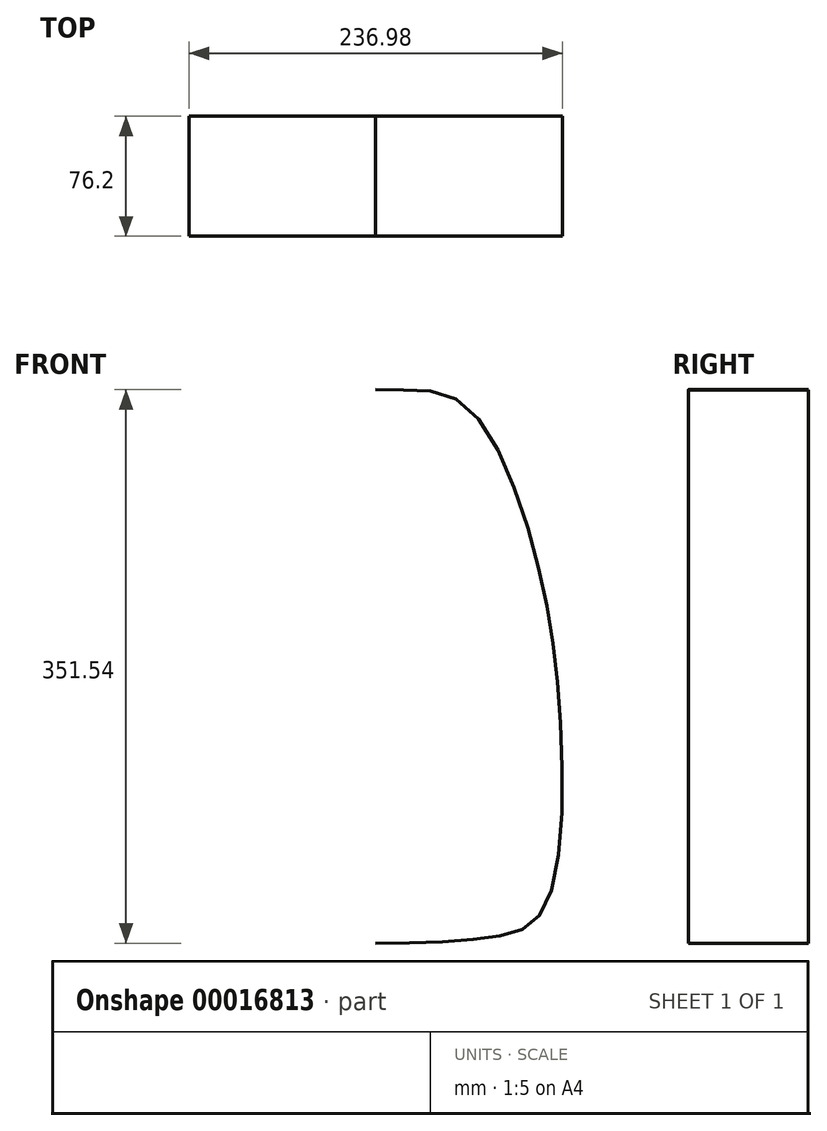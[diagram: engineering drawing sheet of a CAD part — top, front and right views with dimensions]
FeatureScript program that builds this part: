
annotation { "Feature Type Name" : "Feature", "Feature Type Description" : "" }
export const myFeature = defineFeature(function(context is Context, id is Id, definition is map)
    precondition{}
    {
        {
            var Q0;
            Q0=qCreatedBy(makeId("Front.planeOp"),FACE);
            var sketch = newSketch(context, id + "F0", { "sketchPlane" : qUnion([Q0])});
            skLineSegment(sketch, "E0.rect.bottom", {"start": v(127, -177.8) * mm, "end": v(-127, -177.8) * mm, "construction": true});
            skLineSegment(sketch, "E0.rect.top", {"start": v(127, 177.8) * mm, "end": v(-127, 177.8) * mm, "construction": true});
            skLineSegment(sketch, "E0.rect.left", {"start": v(127, -177.8) * mm, "end": v(127, 177.8) * mm, "construction": true});
            skLineSegment(sketch, "E0.rect.right", {"start": v(-127, -177.8) * mm, "end": v(-127, 177.8) * mm, "construction": true});
            skPoint(sketch, "E0.rect.middle", {"position": v(0, 0) * mm});
            skLineSegment(sketch, "E1", {"start": v(0, 177.8) * mm, "end": v(0, -177.8) * mm, "construction": true});
            skFitSpline(sketch, "E2", {"points": [v(0, 177.8) * mm, v(52.82, 170.8) * mm, v(100.33, 76.63) * mm, v(117.44, -36.52) * mm, v(106.7, -152.11) * mm, v(73.54, -169.94) * mm, v(0, -173.74) * mm], "startDerivative": vector(407.17, -25.83) * mm, "endDerivative": vector(-498.99, 0) * mm});
            skFitSpline(sketch, "E3.MirrorCS", {"points": [v(0, 177.8) * mm, v(-52.82, 170.8) * mm, v(-100.33, 76.63) * mm, v(-117.44, -36.52) * mm, v(-106.7, -152.11) * mm, v(-73.54, -169.94) * mm, v(0, -173.74) * mm], "startDerivative": vector(-407.17, -25.83) * mm, "endDerivative": vector(498.99, 0) * mm});
            skSolve(sketch);
        }
        {
            var Q0;
            Q0 = qConstructionFilter(qBodyType(qCreatedBy(id + "F0" ,EDGE), BodyType.WIRE), ConstructionObject.NO);
            extrude(context, id + "F1", {"bodyType" : ToolBodyType.SURFACE, "surfaceEntities" : qUnion([Q0]), "depth" : 76.2 * mm});
        }
    });
